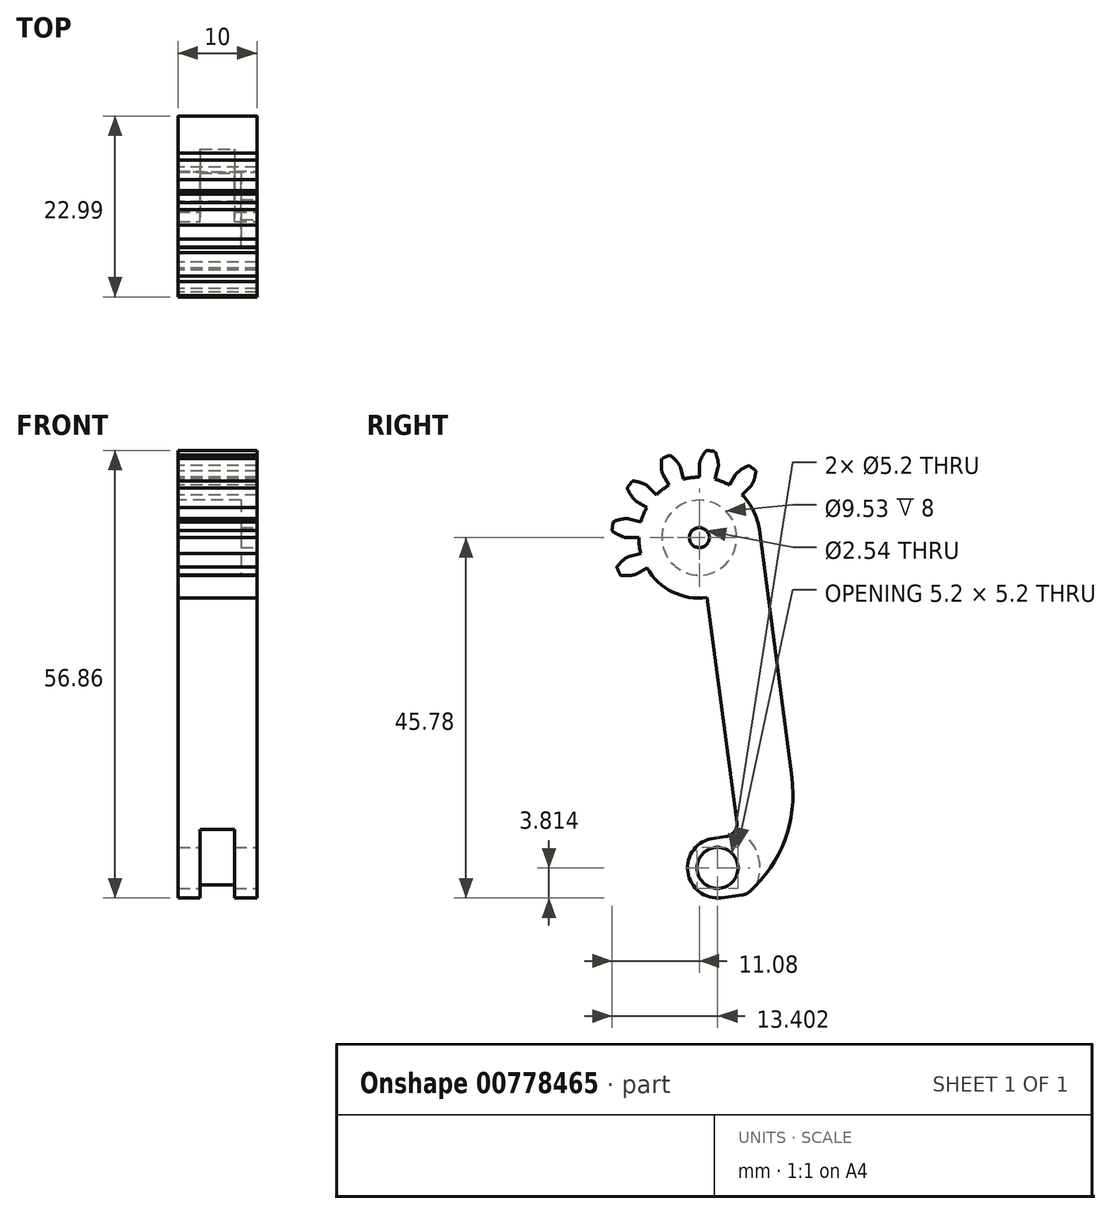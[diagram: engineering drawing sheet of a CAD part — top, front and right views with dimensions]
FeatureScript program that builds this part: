
annotation { "Feature Type Name" : "Feature", "Feature Type Description" : "" }
export const myFeature = defineFeature(function(context is Context, id is Id, definition is map)
    precondition{}
    {
        {
            assignVariable(context, id + "F0", {"name" : "NumberTeeth", "anyValue" : 12});
        }
        {
            assignVariable(context, id + "F1", {"name" : "GearThickness", "anyValue" : 10 * mm});
        }
        {
            var Q0;
            Q0=qCreatedBy(makeId("Right.planeOp"),FACE);
            var sketch = newSketch(context, id + "F2", { "sketchPlane" : qUnion([Q0])});
            skCircle(sketch, "E0", {"center": v(0, 0) * mm, "radius": 7.69 * mm});
            skCircle(sketch, "E1", {"center": v(0, 0) * mm, "radius": 9.22 * mm, "construction": true});
            skCircle(sketch, "E2", {"center": v(0, 0) * mm, "radius": 9.53 * mm, "construction": true});
            skCircle(sketch, "E3", {"center": v(0, 0) * mm, "radius": 11.11 * mm});
            skLineSegment(sketch, "E4", {"start": v(0, 0) * mm, "end": v(-9.22, 0) * mm, "construction": true});
            skLineSegment(sketch, "E5.1.0", {"start": v(0, 0) * mm, "end": v(-9.21, 0.46) * mm, "construction": true});
            skLineSegment(sketch, "E5.2.0", {"start": v(0, 0) * mm, "end": v(-9.18, 0.92) * mm, "construction": true});
            skLineSegment(sketch, "E5.3.0", {"start": v(0, 0) * mm, "end": v(-9.12, 1.38) * mm, "construction": true});
            skLineSegment(sketch, "E5.4.0", {"start": v(0, 0) * mm, "end": v(-9.04, 1.83) * mm, "construction": true});
            skLineSegment(sketch, "E5.5.0", {"start": v(0, 0) * mm, "end": v(-8.93, 2.28) * mm, "construction": true});
            skLineSegment(sketch, "E5.6.0", {"start": v(0, 0) * mm, "end": v(-8.8, 2.73) * mm, "construction": true});
            skLineSegment(sketch, "E5.7.0", {"start": v(0, 0) * mm, "end": v(-8.66, 3.16) * mm, "construction": true});
            skLineSegment(sketch, "E5.8.0", {"start": v(0, 0) * mm, "end": v(-8.5, 3.6) * mm, "construction": true});
            skLineSegment(sketch, "E5.9.0", {"start": v(0, 0) * mm, "end": v(-8.3, 4.01) * mm, "construction": true});
            skLineSegment(sketch, "E5.10.0", {"start": v(0, 0) * mm, "end": v(-8.1, 4.42) * mm, "construction": true});
            skLineSegment(sketch, "E5.11.0", {"start": v(0, 0) * mm, "end": v(-7.86, 4.82) * mm, "construction": true});
            skLineSegment(sketch, "E5.12.0", {"start": v(0, 0) * mm, "end": v(-7.61, 5.2) * mm, "construction": true});
            skLineSegment(sketch, "E5.13.0", {"start": v(0, 0) * mm, "end": v(-7.34, 5.58) * mm, "construction": true});
            skLineSegment(sketch, "E5.14.0", {"start": v(0, 0) * mm, "end": v(-7.05, 5.94) * mm, "construction": true});
            skLineSegment(sketch, "E5.anchor2", {"start": v(0, 0) * mm, "end": v(-7.05, 5.94) * mm, "construction": true});
            skLineSegment(sketch, "E6", {"start": v(-9.21, 0.46) * mm, "end": v(-9.23, 0) * mm, "construction": true});
            skLineSegment(sketch, "E7", {"start": v(-9.18, 0.92) * mm, "end": v(-9.27, 0) * mm, "construction": true});
            skLineSegment(sketch, "E8", {"start": v(-9.12, 1.38) * mm, "end": v(-9.32, 0.01) * mm, "construction": true});
            skLineSegment(sketch, "E9", {"start": v(-8.93, 2.28) * mm, "end": v(-9.5, 0.05) * mm, "construction": true});
            skLineSegment(sketch, "E10", {"start": v(-8.8, 2.73) * mm, "end": v(-9.63, 0.08) * mm, "construction": true});
            skLineSegment(sketch, "E11", {"start": v(-8.66, 3.16) * mm, "end": v(-9.77, 0.13) * mm, "construction": true});
            skLineSegment(sketch, "E12", {"start": v(-8.5, 3.6) * mm, "end": v(-9.93, 0.2) * mm, "construction": true});
            skLineSegment(sketch, "E13", {"start": v(-8.3, 4.01) * mm, "end": v(-10.1, 0.27) * mm, "construction": true});
            skLineSegment(sketch, "E14", {"start": v(-8.1, 4.42) * mm, "end": v(-10.3, 0.37) * mm, "construction": true});
            skLineSegment(sketch, "E15", {"start": v(-7.86, 4.82) * mm, "end": v(-10.51, 0.5) * mm, "construction": true});
            skLineSegment(sketch, "E16", {"start": v(-9.04, 1.83) * mm, "end": v(-9.4, 0.02) * mm, "construction": true});
            skLineSegment(sketch, "E17", {"start": v(-7.61, 5.2) * mm, "end": v(-10.74, 0.64) * mm, "construction": true});
            skLineSegment(sketch, "E18", {"start": v(-7.34, 5.58) * mm, "end": v(-10.97, 0.8) * mm, "construction": true});
            skLineSegment(sketch, "E19", {"start": v(-7.05, 5.94) * mm, "end": v(-11.21, 1) * mm, "construction": true});
            skLineSegment(sketch, "E20", {"start": v(0, 0) * mm, "end": v(-9.14, 1.2) * mm, "construction": true});
            skLineSegment(sketch, "E21", {"start": v(-7.69, 0) * mm, "end": v(-9.22, 0) * mm});
            skLineSegment(sketch, "E22.MirrorCS", {"start": v(-7.43, 1.99) * mm, "end": v(-8.9, 2.39) * mm});
            skFitSpline(sketch, "E23", {"points": [v(-9.22, 0) * mm, v(-9.23, 0) * mm, v(-9.27, 0) * mm, v(-9.32, 0.01) * mm, v(-9.4, 0.02) * mm, v(-9.5, 0.05) * mm, v(-9.63, 0.08) * mm, v(-9.77, 0.13) * mm, v(-9.93, 0.2) * mm, v(-10.1, 0.27) * mm, v(-10.3, 0.37) * mm, v(-10.51, 0.5) * mm, v(-10.74, 0.64) * mm, v(-10.97, 0.8) * mm, v(-11.21, 1) * mm], "startDerivative": vector(-0.86, 0) * mm, "endDerivative": vector(-1.03, 0.87) * mm});
            skLineSegment(sketch, "E24", {"start": v(-11.21, 1) * mm, "end": v(-16.27, 5.26) * mm, "construction": true});
            skFitSpline(sketch, "E25.MirrorCS", {"points": [v(-8.9, 2.39) * mm, v(-8.92, 2.39) * mm, v(-8.95, 2.4) * mm, v(-9, 2.4) * mm, v(-9.1, 2.41) * mm, v(-9.2, 2.41) * mm, v(-9.32, 2.41) * mm, v(-9.47, 2.4) * mm, v(-9.64, 2.38) * mm, v(-9.84, 2.35) * mm, v(-10.05, 2.3) * mm, v(-10.28, 2.24) * mm, v(-10.54, 2.16) * mm, v(-10.8, 2.06) * mm, v(-11.09, 1.93) * mm], "startDerivative": vector(-0.83, 0.22) * mm, "endDerivative": vector(-1.22, -0.57) * mm});
            skSolve(sketch);
        }
        {
            var Q0;
            {var subQ0=sQuery(id+"F2.wireOp",EDGE,"E0");var subQ27=makeQuery(id+"F2.imprint","INTERSECT",VERTEX,{"derivedFrom":[subQ0,sQuery(id+"F2.wireOp",EDGE,"10ea1024-8cf5-41f5-a75f-a634b86921f3.10.0")]});Q0=makeQuery(id+"F2.imprint","IMPRINT",FACE,{"disambiguationData":[TD([[makeQuery(id+"F2.imprint","IMPRINT",EDGE,{"disambiguationData":[TD([[subQ27,-1.0]])],"derivedFrom":subQ0}),1.0]])]});}
            var Q1;
            {var subQ0=sQuery(id+"F2.wireOp",EDGE,"10ea1024-8cf5-41f5-a75f-a634b86921f3.1.0");Q1=makeQuery(id+"F2.imprint","IMPRINT",FACE,{"disambiguationData":[TD([[makeQuery(id+"F2.imprint","IMPRINT",EDGE,{"derivedFrom":subQ0}),-1.0]])]});}
            var Q2;
            {var subQ7=sQuery(id+"F2.wireOp",EDGE,"10ea1024-8cf5-41f5-a75f-a634b86921f3.2.0");Q2=makeQuery(id+"F2.imprint","IMPRINT",FACE,{"disambiguationData":[TD([[makeQuery(id+"F2.imprint","IMPRINT",EDGE,{"derivedFrom":subQ7}),-1.0]])]});}
            var Q3;
            {var subQ8=sQuery(id+"F2.wireOp",EDGE,"10ea1024-8cf5-41f5-a75f-a634b86921f3.3.0");Q3=makeQuery(id+"F2.imprint","IMPRINT",FACE,{"disambiguationData":[TD([[makeQuery(id+"F2.imprint","IMPRINT",EDGE,{"derivedFrom":subQ8}),-1.0]])]});}
            var Q4;
            {var subQ2=sQuery(id+"F2.wireOp",EDGE,"10ea1024-8cf5-41f5-a75f-a634b86921f3.4.0");Q4=makeQuery(id+"F2.imprint","IMPRINT",FACE,{"disambiguationData":[TD([[makeQuery(id+"F2.imprint","IMPRINT",EDGE,{"derivedFrom":subQ2}),-1.0]])]});}
            var Q5;
            {var subQ8=sQuery(id+"F2.wireOp",EDGE,"10ea1024-8cf5-41f5-a75f-a634b86921f3.5.0");Q5=makeQuery(id+"F2.imprint","IMPRINT",FACE,{"disambiguationData":[TD([[makeQuery(id+"F2.imprint","IMPRINT",EDGE,{"derivedFrom":subQ8}),-1.0]])]});}
            var Q6;
            {var subQ3=sQuery(id+"F2.wireOp",EDGE,"10ea1024-8cf5-41f5-a75f-a634b86921f3.6.0");Q6=makeQuery(id+"F2.imprint","IMPRINT",FACE,{"disambiguationData":[TD([[makeQuery(id+"F2.imprint","IMPRINT",EDGE,{"derivedFrom":subQ3}),-1.0]])]});}
            var Q7;
            {var subQ0=sQuery(id+"F2.wireOp",EDGE,"10ea1024-8cf5-41f5-a75f-a634b86921f3.7.0");Q7=makeQuery(id+"F2.imprint","IMPRINT",FACE,{"disambiguationData":[TD([[makeQuery(id+"F2.imprint","IMPRINT",EDGE,{"derivedFrom":subQ0}),-1.0]])]});}
            var Q8;
            {var subQ5=sQuery(id+"F2.wireOp",EDGE,"10ea1024-8cf5-41f5-a75f-a634b86921f3.8.0");Q8=makeQuery(id+"F2.imprint","IMPRINT",FACE,{"disambiguationData":[TD([[makeQuery(id+"F2.imprint","IMPRINT",EDGE,{"derivedFrom":subQ5}),-1.0]])]});}
            var Q9;
            {var subQ1=sQuery(id+"F2.wireOp",EDGE,"10ea1024-8cf5-41f5-a75f-a634b86921f3.9.0");Q9=makeQuery(id+"F2.imprint","IMPRINT",FACE,{"disambiguationData":[TD([[makeQuery(id+"F2.imprint","IMPRINT",EDGE,{"derivedFrom":subQ1}),-1.0]])]});}
            var Q10;
            {var subQ5=sQuery(id+"F2.wireOp",EDGE,"10ea1024-8cf5-41f5-a75f-a634b86921f3.10.0");Q10=makeQuery(id+"F2.imprint","IMPRINT",FACE,{"disambiguationData":[TD([[makeQuery(id+"F2.imprint","IMPRINT",EDGE,{"derivedFrom":subQ5}),-1.0]])]});}
            var Q11;
            {var subQ8=sQuery(id+"F2.wireOp",EDGE,"10ea1024-8cf5-41f5-a75f-a634b86921f3.11.0");Q11=makeQuery(id+"F2.imprint","IMPRINT",FACE,{"disambiguationData":[TD([[makeQuery(id+"F2.imprint","IMPRINT",EDGE,{"derivedFrom":subQ8}),-1.0]])]});}
            var Q12;
            {var subQ2=sQuery(id+"F2.wireOp",EDGE,"10ea1024-8cf5-41f5-a75f-a634b86921f3.12.0");Q12=makeQuery(id+"F2.imprint","IMPRINT",FACE,{"disambiguationData":[TD([[makeQuery(id+"F2.imprint","IMPRINT",EDGE,{"derivedFrom":subQ2}),-1.0]])]});}
            var Q13;
            {var subQ3=sQuery(id+"F2.wireOp",EDGE,"10ea1024-8cf5-41f5-a75f-a634b86921f3.13.0");Q13=makeQuery(id+"F2.imprint","IMPRINT",FACE,{"disambiguationData":[TD([[makeQuery(id+"F2.imprint","IMPRINT",EDGE,{"derivedFrom":subQ3}),-1.0]])]});}
            var Q14;
            {var subQ0=sQuery(id+"F2.wireOp",EDGE,"10ea1024-8cf5-41f5-a75f-a634b86921f3.14.0");Q14=makeQuery(id+"F2.imprint","IMPRINT",FACE,{"disambiguationData":[TD([[makeQuery(id+"F2.imprint","IMPRINT",EDGE,{"derivedFrom":subQ0}),-1.0]])]});}
            var Q15;
            {var subQ6=sQuery(id+"F2.wireOp",EDGE,"10ea1024-8cf5-41f5-a75f-a634b86921f3.15.0");Q15=makeQuery(id+"F2.imprint","IMPRINT",FACE,{"disambiguationData":[TD([[makeQuery(id+"F2.imprint","IMPRINT",EDGE,{"derivedFrom":subQ6}),-1.0]])]});}
            var Q16;
            {var subQ5=sQuery(id+"F2.wireOp",EDGE,"10ea1024-8cf5-41f5-a75f-a634b86921f3.16.0");Q16=makeQuery(id+"F2.imprint","IMPRINT",FACE,{"disambiguationData":[TD([[makeQuery(id+"F2.imprint","IMPRINT",EDGE,{"derivedFrom":subQ5}),-1.0]])]});}
            var Q17;
            {var subQ7=sQuery(id+"F2.wireOp",EDGE,"10ea1024-8cf5-41f5-a75f-a634b86921f3.17.0");Q17=makeQuery(id+"F2.imprint","IMPRINT",FACE,{"disambiguationData":[TD([[makeQuery(id+"F2.imprint","IMPRINT",EDGE,{"derivedFrom":subQ7}),-1.0]])]});}
            var Q18;
            {var subQ5=sQuery(id+"F2.wireOp",EDGE,"10ea1024-8cf5-41f5-a75f-a634b86921f3.18.0");Q18=makeQuery(id+"F2.imprint","IMPRINT",FACE,{"disambiguationData":[TD([[makeQuery(id+"F2.imprint","IMPRINT",EDGE,{"derivedFrom":subQ5}),-1.0]])]});}
            var Q19;
            {var subQ8=sQuery(id+"F2.wireOp",EDGE,"10ea1024-8cf5-41f5-a75f-a634b86921f3.19.0");Q19=makeQuery(id+"F2.imprint","IMPRINT",FACE,{"disambiguationData":[TD([[makeQuery(id+"F2.imprint","IMPRINT",EDGE,{"derivedFrom":subQ8}),-1.0]])]});}
            var Q20;
            {var subQ8=sQuery(id+"F2.wireOp",EDGE,"E21");Q20=makeQuery(id+"F2.imprint","IMPRINT",FACE,{"disambiguationData":[TD([[makeQuery(id+"F2.imprint","IMPRINT",EDGE,{"derivedFrom":subQ8}),-1.0]])]});}
            extrude(context, id + "F3", {"entities" : qUnion([Q0, Q1, Q2, Q3, Q4, Q5, Q6, Q7, Q8, Q9, Q10, Q11, Q12, Q13, Q14, Q15, Q16, Q17, Q18, Q19, Q20]), "depth" : (getVariable(context, 'GearThickness')), "offsetDistance" : 25.4 * mm});
        }
        {
            var Q0;
            Q0=makeQuery(id+"F3.opExtrude","SWEPT_FACE",FACE,{"disambiguationData":[OSD([sQuery(id+"F2.wireOp",EDGE,"E25.MirrorCS")])]});
            var Q1;
            Q1=makeQuery(id+"F3.opExtrude","SWEPT_FACE",FACE,{"disambiguationData":[OSD([sQuery(id+"F2.wireOp",EDGE,"E23")])]});
            var Q2;
            Q2=makeQuery(id+"F3.opExtrude","SWEPT_FACE",FACE,{"disambiguationData":[OSD([sQuery(id+"F2.wireOp",EDGE,"E3")])]});
            var Q3;
            Q3=makeQuery(id+"F3.opExtrude","SWEPT_FACE",FACE,{"disambiguationData":[OSD([sQuery(id+"F2.wireOp",EDGE,"E22.MirrorCS")])]});
            var Q4;
            Q4=makeQuery(id+"F3.opExtrude","SWEPT_FACE",FACE,{"disambiguationData":[OSD([sQuery(id+"F2.wireOp",EDGE,"E21")])]});
            var Q5;
            Q5=makeQuery(id+"F3.opExtrude","SWEPT_FACE",FACE,{"disambiguationData":[OSD([sQuery(id+"F2.wireOp",EDGE,"E0")])]});
            circularPattern(context, id + "F4", {"faces" : qUnion([Q0, Q1, Q2, Q3, Q4]), "axis" : qUnion([Q5]), "angle" : 360 * degree, "instanceCount" : getVariable(context, 'NumberTeeth'), "equalSpace" : true, "patternType" : PatternType.FACE});
        }
        {
            var Q0;
            Q0=makeQuery(id+"F3.opExtrude","CAP_FACE",FACE,{"disambiguationData":[OSD([sQuery(id+"F2.wireOp",EDGE,"E0"),sQuery(id+"F2.wireOp",EDGE,"E3"),sQuery(id+"F2.wireOp",EDGE,"E21"),sQuery(id+"F2.wireOp",EDGE,"E22.MirrorCS"),sQuery(id+"F2.wireOp",EDGE,"E23"),sQuery(id+"F2.wireOp",EDGE,"E25.MirrorCS")])],"isStart":true});
            var sketch = newSketch(context, id + "F5", { "sketchPlane" : qUnion([Q0])});
            skCircle(sketch, "E26", {"center": v(0, 0) * mm, "radius": 4.76 * mm});
            skSolve(sketch);
        }
        {
            var Q0;
            Q0 = qSketchRegion(id + "F5", true);
            extrude(context, id + "F6", {"entities" : qUnion([Q0]), "operationType" : NewBodyOperationType.REMOVE, "oppositeDirection" : true, "depth" : 8 * mm, "offsetDistance" : 25.4 * mm});
        }
        {
            var Q0;
            Q0=makeQuery(id+"F3.opExtrude","CAP_FACE",FACE,{"disambiguationData":[OSD([sQuery(id+"F2.wireOp",EDGE,"E0"),sQuery(id+"F2.wireOp",EDGE,"E3"),sQuery(id+"F2.wireOp",EDGE,"E21"),sQuery(id+"F2.wireOp",EDGE,"E22.MirrorCS"),sQuery(id+"F2.wireOp",EDGE,"E23"),sQuery(id+"F2.wireOp",EDGE,"E25.MirrorCS")])],"isStart":false});
            var sketch = newSketch(context, id + "F7", { "sketchPlane" : qUnion([Q0])});
            skCircle(sketch, "E27", {"center": v(0, 0) * mm, "radius": 1.27 * mm});
            skSolve(sketch);
        }
        {
            var Q0;
            Q0 = qSketchRegion(id + "F7", true);
            extrude(context, id + "F8", {"entities" : qUnion([Q0]), "operationType" : NewBodyOperationType.REMOVE, "oppositeDirection" : true, "depth" : 25.4 * mm, "offsetDistance" : 25.4 * mm});
        }
        {
            var Q0;
            Q0=makeQuery(id+"F3.opExtrude","CAP_FACE",FACE,{"disambiguationData":[OSD([sQuery(id+"F2.wireOp",EDGE,"E0"),sQuery(id+"F2.wireOp",EDGE,"E3"),sQuery(id+"F2.wireOp",EDGE,"E21"),sQuery(id+"F2.wireOp",EDGE,"E22.MirrorCS"),sQuery(id+"F2.wireOp",EDGE,"E23"),sQuery(id+"F2.wireOp",EDGE,"E25.MirrorCS")])],"isStart":false});
            var sketch = newSketch(context, id + "F9", { "sketchPlane" : qUnion([Q0])});
            skCircle(sketch, "E28", {"center": v(0, 0) * mm, "radius": 9.92 * mm, "construction": true});
            skLineSegment(sketch, "E29", {"start": v(-7.62, -1) * mm, "end": v(7.62, 1) * mm, "construction": true});
            skLineSegment(sketch, "E30", {"start": v(6.43, -2.12) * mm, "end": v(-6.66, -3.84) * mm});
            skArc(sketch, "E31", {"start": v(-6.66, -3.84) * mm, "mid": v(2.26, -17.2) * mm, "end": v(7.43, -1.99) * mm});
            skArc(sketch, "E32", {"start": v(3.84, -6.66) * mm, "mid": v(15.27, -2.01) * mm, "end": v(5.44, 5.44) * mm});
            skLineSegment(sketch, "E33", {"start": v(5.44, 5.44) * mm, "end": v(6.43, -2.12) * mm});
            skSolve(sketch);
        }
        {
            var Q0;
            Q0 = qSketchRegion(id + "F9", true);
            extrude(context, id + "F10", {"entities" : qUnion([Q0]), "operationType" : NewBodyOperationType.REMOVE, "oppositeDirection" : true, "depth" : 25.4 * mm, "offsetDistance" : 25.4 * mm});
        }
        {
            var Q0;
            Q0=makeQuery(id+"F3.opExtrude","CAP_FACE",FACE,{"disambiguationData":[OSD([sQuery(id+"F2.wireOp",EDGE,"E0"),sQuery(id+"F2.wireOp",EDGE,"E3"),sQuery(id+"F2.wireOp",EDGE,"E21"),sQuery(id+"F2.wireOp",EDGE,"E22.MirrorCS"),sQuery(id+"F2.wireOp",EDGE,"E23"),sQuery(id+"F2.wireOp",EDGE,"E25.MirrorCS")])],"isStart":true});
            var sketch = newSketch(context, id + "F11", { "sketchPlane" : qUnion([Q0])});
            skCircle(sketch, "E34", {"center": v(0, 0) * mm, "radius": 4.76 * mm});
            skCircle(sketch, "E35", {"center": v(0, 0) * mm, "radius": 9.53 * mm, "construction": true});
            skCircle(sketch, "E36", {"center": v(0, 0) * mm, "radius": 7.69 * mm, "construction": true});
            skLineSegment(sketch, "E37", {"start": v(7.62, -1) * mm, "end": v(-7.62, 1) * mm, "construction": true});
            skLineSegment(sketch, "E38", {"start": v(-1.5, -11.33) * mm, "end": v(0, 0) * mm, "construction": true});
            skArc(sketch, "E39", {"start": v(-5.44, 5.44) * mm, "mid": v(-6.9, 3.4) * mm, "end": v(-7.62, 1) * mm});
            skArc(sketch, "E40", {"start": v(6.66, -3.84) * mm, "mid": v(3.4, -6.9) * mm, "end": v(-1, -7.62) * mm});
            skLineSegment(sketch, "E41", {"start": v(-1, -7.62) * mm, "end": v(-8.63, -6.62) * mm});
            skLineSegment(sketch, "E42", {"start": v(-7.62, 1) * mm, "end": v(-8.63, -6.62) * mm});
            skSolve(sketch);
        }
        {
            var Q0;
            Q0=makeQuery(id+"F11.imprint","IMPRINT",FACE,{"disambiguationData":[TD([[makeQuery(id+"F11.imprint","IMPRINT",EDGE,{"derivedFrom":sQuery(id+"F11.wireOp",EDGE,"E39")}),1.0]])]});
            extrude(context, id + "F12", {"entities" : qUnion([Q0]), "oppositeDirection" : true, "depth" : 10 * mm, "offsetDistance" : 25.4 * mm});
        }
        {
            var Q0;
            Q0=makeQuery(id+"F3.opExtrude","SWEPT_BODY",BODY,{"disambiguationData":[OSD([sQuery(id+"F2.wireOp",EDGE,"E0"),sQuery(id+"F2.wireOp",EDGE,"E3"),sQuery(id+"F2.wireOp",EDGE,"E21"),sQuery(id+"F2.wireOp",EDGE,"E22.MirrorCS"),sQuery(id+"F2.wireOp",EDGE,"E23"),sQuery(id+"F2.wireOp",EDGE,"E25.MirrorCS")])]});
            var Q1;
            Q1=makeQuery(id+"F12.opExtrude","SWEPT_BODY",BODY,{"disambiguationData":[OSD([sQuery(id+"F2.wireOp",EDGE,"E0"),sQuery(id+"F2.wireOp",EDGE,"E3"),sQuery(id+"F2.wireOp",EDGE,"E21"),sQuery(id+"F2.wireOp",EDGE,"E22.MirrorCS"),sQuery(id+"F2.wireOp",EDGE,"E23"),sQuery(id+"F2.wireOp",EDGE,"E25.MirrorCS"),sQuery(id+"F9.wireOp",EDGE,"E30"),sQuery(id+"F9.wireOp",EDGE,"E33"),sQuery(id+"F11.wireOp",EDGE,"E34"),sQuery(id+"F11.wireOp",EDGE,"E39"),sQuery(id+"F11.wireOp",EDGE,"E40"),sQuery(id+"F11.wireOp",EDGE,"E41"),sQuery(id+"F11.wireOp",EDGE,"E42")])]});
            booleanBodies(context, id + "F13", {"operationType" : BooleanOperationType.UNION, "tools" : qUnion([Q0, Q1])});
        }
        {
            var Q0;
            {var subQ0=sQuery(id+"F2.wireOp",EDGE,"E25.MirrorCS");var subQ1=sQuery(id+"F2.wireOp",EDGE,"E23");var subQ2=sQuery(id+"F2.wireOp",EDGE,"E22.MirrorCS");var subQ3=sQuery(id+"F2.wireOp",EDGE,"E21");var subQ4=sQuery(id+"F2.wireOp",EDGE,"E3");var subQ5=sQuery(id+"F2.wireOp",EDGE,"E0");Q0=makeQuery(id+"F13.opBoolean","MERGE",FACE,{"derivedFrom":[makeQuery(id+"F3.opExtrude","CAP_FACE",FACE,{"disambiguationData":[OSD([subQ5,subQ4,subQ3,subQ2,subQ1,subQ0])],"isStart":false}),makeQuery(id+"F12.opExtrude","CAP_FACE",FACE,{"disambiguationData":[OSD([subQ5,subQ4,subQ3,subQ2,subQ1,subQ0,sQuery(id+"F9.wireOp",EDGE,"E30"),sQuery(id+"F9.wireOp",EDGE,"E33"),sQuery(id+"F11.wireOp",EDGE,"E34"),sQuery(id+"F11.wireOp",EDGE,"E39"),sQuery(id+"F11.wireOp",EDGE,"E40"),sQuery(id+"F11.wireOp",EDGE,"E41"),sQuery(id+"F11.wireOp",EDGE,"E42")])],"isStart":false})]});}
            var sketch = newSketch(context, id + "F14", { "sketchPlane" : qUnion([Q0])});
            skLineSegment(sketch, "E43", {"start": v(-3.33, -3.4) * mm, "end": v(4.1, -2.43) * mm});
            skArc(sketch, "E44", {"start": v(-3.33, -3.4) * mm, "mid": v(0.62, -4.72) * mm, "end": v(4.1, -2.43) * mm});
            skSolve(sketch);
        }
        {
            var Q0;
            Q0 = qSketchRegion(id + "F14", true);
            extrude(context, id + "F15", {"entities" : qUnion([Q0]), "oppositeDirection" : true, "depth" : 2 * mm, "offsetDistance" : 25.4 * mm});
        }
        {
            var Q0;
            Q0=makeQuery(id+"F3.opExtrude","SWEPT_BODY",BODY,{"disambiguationData":[OSD([sQuery(id+"F2.wireOp",EDGE,"E0"),sQuery(id+"F2.wireOp",EDGE,"E3"),sQuery(id+"F2.wireOp",EDGE,"E21"),sQuery(id+"F2.wireOp",EDGE,"E22.MirrorCS"),sQuery(id+"F2.wireOp",EDGE,"E23"),sQuery(id+"F2.wireOp",EDGE,"E25.MirrorCS")])]});
            var Q1;
            Q1=makeQuery(id+"F15.opExtrude","SWEPT_BODY",BODY,{"disambiguationData":[OSD([sQuery(id+"F14.wireOp",EDGE,"E43"),sQuery(id+"F14.wireOp",EDGE,"E44")])]});
            booleanBodies(context, id + "F16", {"operationType" : BooleanOperationType.UNION, "tools" : qUnion([Q0, Q1])});
        }
        {
            var Q0;
            {var subQ0=sQuery(id+"F2.wireOp",EDGE,"E25.MirrorCS");var subQ1=sQuery(id+"F2.wireOp",EDGE,"E23");var subQ2=sQuery(id+"F2.wireOp",EDGE,"E22.MirrorCS");var subQ3=sQuery(id+"F2.wireOp",EDGE,"E21");var subQ4=sQuery(id+"F2.wireOp",EDGE,"E3");var subQ5=sQuery(id+"F2.wireOp",EDGE,"E0");Q0=makeQuery(id+"F16.opBoolean","MERGE",FACE,{"derivedFrom":[makeQuery(id+"F13.opBoolean","MERGE",FACE,{"derivedFrom":[makeQuery(id+"F3.opExtrude","CAP_FACE",FACE,{"disambiguationData":[OSD([subQ5,subQ4,subQ3,subQ2,subQ1,subQ0])],"isStart":false}),makeQuery(id+"F12.opExtrude","CAP_FACE",FACE,{"disambiguationData":[OSD([subQ5,subQ4,subQ3,subQ2,subQ1,subQ0,sQuery(id+"F9.wireOp",EDGE,"E30"),sQuery(id+"F9.wireOp",EDGE,"E33"),sQuery(id+"F11.wireOp",EDGE,"E34"),sQuery(id+"F11.wireOp",EDGE,"E39"),sQuery(id+"F11.wireOp",EDGE,"E40"),sQuery(id+"F11.wireOp",EDGE,"E41"),sQuery(id+"F11.wireOp",EDGE,"E42")])],"isStart":false})]}),makeQuery(id+"F15.opExtrude","CAP_FACE",FACE,{"disambiguationData":[OSD([sQuery(id+"F14.wireOp",EDGE,"E43"),sQuery(id+"F14.wireOp",EDGE,"E44")])],"isStart":true})]});}
            var sketch = newSketch(context, id + "F17", { "sketchPlane" : qUnion([Q0])});
            skLineSegment(sketch, "E45", {"start": v(7.62, 1) * mm, "end": v(11.77, -30.47) * mm});
            skLineSegment(sketch, "E46", {"start": v(1, -7.62) * mm, "end": v(4.77, -36.2) * mm});
            skLineSegment(sketch, "E47", {"start": v(-9.44, -1.24) * mm, "end": v(9.44, 1.24) * mm, "construction": true});
            skLineSegment(sketch, "E48", {"start": v(-9.44, -1.24) * mm, "end": v(-1.91, -58.43) * mm, "construction": true});
            skCircle(sketch, "E49", {"center": v(0, 0) * mm, "radius": 9.53 * mm, "construction": true});
            skLineSegment(sketch, "E50", {"start": v(-1.98, -9.32) * mm, "end": v(2.32, -41.97) * mm, "construction": true});
            skLineSegment(sketch, "E51", {"start": v(3.4, -37.98) * mm, "end": v(1.83, -38.19) * mm});
            skCircle(sketch, "E52", {"center": v(2.32, -41.97) * mm, "radius": 2.6 * mm});
            skArc(sketch, "E53", {"start": v(1.83, -38.19) * mm, "mid": v(-1.45, -42.46) * mm, "end": v(2.82, -45.74) * mm});
            skLineSegment(sketch, "E54", {"start": v(2.32, -41.97) * mm, "end": v(4.54, -58.77) * mm, "construction": true});
            skLineSegment(sketch, "E55", {"start": v(2.82, -45.74) * mm, "end": v(5.5, -45.4) * mm});
            skArc(sketch, "E56", {"start": v(6.34, -45) * mm, "mid": v(10.86, -38.41) * mm, "end": v(11.77, -30.47) * mm});
            skPoint(sketch, "E57.visualSharp", {"position": v(5.97, -45.33) * mm});
            skArc(sketch, "E57.filletArc", {"start": v(5.5, -45.4) * mm, "mid": v(5.95, -45.26) * mm, "end": v(6.34, -45) * mm});
            skPoint(sketch, "E58.visualSharp", {"position": v(4.97, -37.77) * mm});
            skArc(sketch, "E58.filletArc", {"start": v(3.4, -37.98) * mm, "mid": v(4.45, -37.37) * mm, "end": v(4.77, -36.2) * mm});
            skSolve(sketch);
        }
        {
            var Q0;
            Q0=makeQuery(id+"F17.imprint","IMPRINT",FACE,{"disambiguationData":[TD([[makeQuery(id+"F17.imprint","IMPRINT",EDGE,{"derivedFrom":sQuery(id+"F17.wireOp",EDGE,"E46")}),1.0]])]});
            extrude(context, id + "F18", {"entities" : qUnion([Q0]), "operationType" : NewBodyOperationType.ADD, "oppositeDirection" : true, "depth" : 10 * mm, "offsetDistance" : 25.4 * mm});
        }
        {
            var Q0;
            Q0=makeQuery(id+"F18.opExtrude","SWEPT_EDGE",EDGE,{"disambiguationData":[OSD([sQuery(id+"F17.wireOp",EDGE,"E51"),sQuery(id+"F17.wireOp",EDGE,"E53")])]});
            var Q1;
            Q1=makeQuery(id+"F18.opExtrude","SWEPT_EDGE",EDGE,{"disambiguationData":[OSD([sQuery(id+"F17.wireOp",EDGE,"E53"),sQuery(id+"F17.wireOp",EDGE,"E55")])]});
            cPlane(context, id + "F19", {"entities" : qUnion([Q0, Q1]), "cplaneType" : CPlaneType.LINE_ANGLE, "offset" : 25.4 * mm, "angle" : 0 * degree, "width" : 152.4 * mm, "height" : 152.4 * mm});
        }
        {
            var Q0;
            Q0=qCreatedBy(id+"F19.planeOp",FACE);
            var sketch = newSketch(context, id + "F20", { "sketchPlane" : qUnion([Q0])});
            skLineSegment(sketch, "E59", {"start": v(1.8, -41.91) * mm, "end": v(-13.34, -41.91) * mm, "construction": true});
            skLineSegment(sketch, "E60.bottom", {"start": v(-7.2, -36.51) * mm, "end": v(-2.8, -36.51) * mm});
            skLineSegment(sketch, "E60.top", {"start": v(-7.2, -41.91) * mm, "end": v(-2.8, -41.91) * mm});
            skLineSegment(sketch, "E60.left", {"start": v(-7.2, -36.51) * mm, "end": v(-7.2, -41.91) * mm});
            skLineSegment(sketch, "E60.right", {"start": v(-2.8, -36.51) * mm, "end": v(-2.8, -41.91) * mm});
            skSolve(sketch);
        }
        {
            var Q0;
            Q0 = qSketchRegion(id + "F20", true);
            var Q1;
            Q1=sQuery(id+"F20.wireOp",EDGE,"E59");
            revolve(context, id + "F21", {"operationType" : NewBodyOperationType.REMOVE, "surfaceOperationType" : NewSurfaceOperationType.NEW, "entities" : qUnion([Q0]), "axis" : qUnion([Q1]), "revolveType" : RevolveType.FULL, "oppositeDirection" : true});
        }
    });
